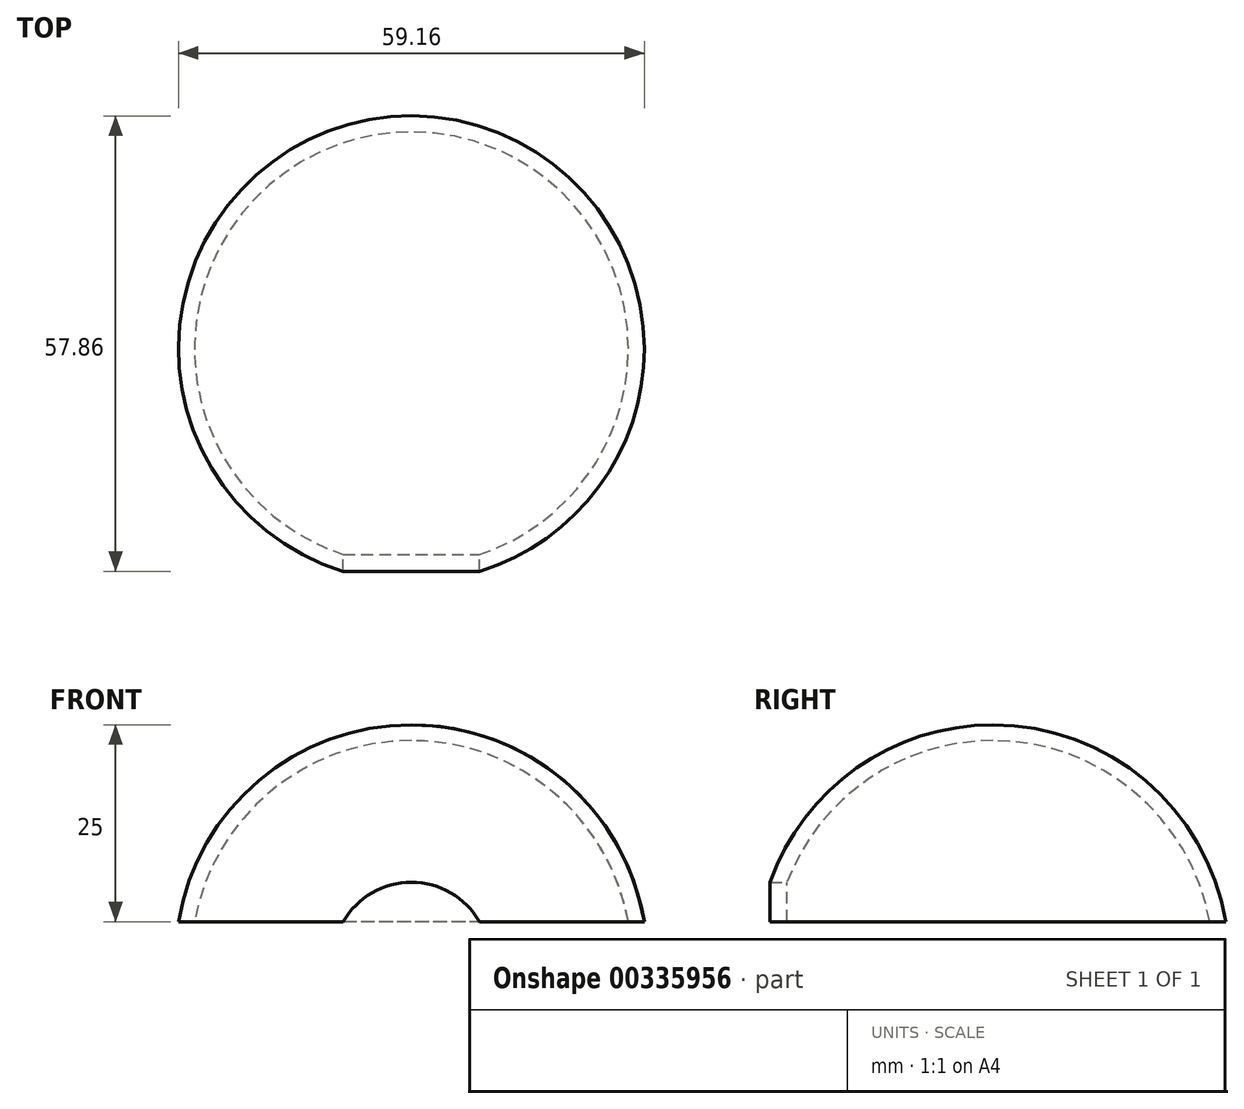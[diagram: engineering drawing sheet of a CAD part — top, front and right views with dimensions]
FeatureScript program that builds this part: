
annotation { "Feature Type Name" : "Feature", "Feature Type Description" : "" }
export const myFeature = defineFeature(function(context is Context, id is Id, definition is map)
    precondition{}
    {
        {
            var Q0;
            Q0=qCreatedBy(makeId("Front.planeOp"),FACE);
            var sketch = newSketch(context, id + "F0", { "sketchPlane" : qUnion([Q0])});
            skArc(sketch, "E0", {"start": v(0, 30) * mm, "mid": v(19.36, 22.91) * mm, "end": v(29.58, 5) * mm});
            skLineSegment(sketch, "E1", {"start": v(0, 30) * mm, "end": v(0, 5) * mm});
            skLineSegment(sketch, "E2", {"start": v(0, 5) * mm, "end": v(29.58, 5) * mm});
            skPoint(sketch, "E3.orphan", {"position": v(0, -30) * mm});
            skSolve(sketch);
        }
        {
            var Q0;
            Q0 = qSketchRegion(id + "F0", true);
            var Q1;
            Q1=sQuery(id+"F0.wireOp",EDGE,"E1");
            revolve(context, id + "F1", {"entities" : qUnion([Q0]), "axis" : qUnion([Q1]), "revolveType" : RevolveType.FULL});
        }
        {
            var Q0;
            Q0=makeQuery(id+"F1.opRevolve","SWEPT_FACE",FACE,{"disambiguationData":[OSD([sQuery(id+"F0.wireOp",EDGE,"E2")])]});
            shell(context, id + "F2", {"entities" : qUnion([Q0]), "thickness" : 2 * mm});
        }
        {
            var Q0;
            Q0=qCreatedBy(makeId("Front.planeOp"),FACE);
            var sketch = newSketch(context, id + "F3", { "sketchPlane" : qUnion([Q0])});
            skCircle(sketch, "E4", {"center": v(0, 0) * mm, "radius": 10 * mm});
            skSolve(sketch);
        }
        {
            var Q0;
            Q0 = qSketchRegion(id + "F3", true);
            extrude(context, id + "F4", {"entities" : qUnion([Q0]), "operationType" : NewBodyOperationType.REMOVE, "endBound" : BoundingType.THROUGH_ALL, "depth" : 25 * mm});
        }
    });
